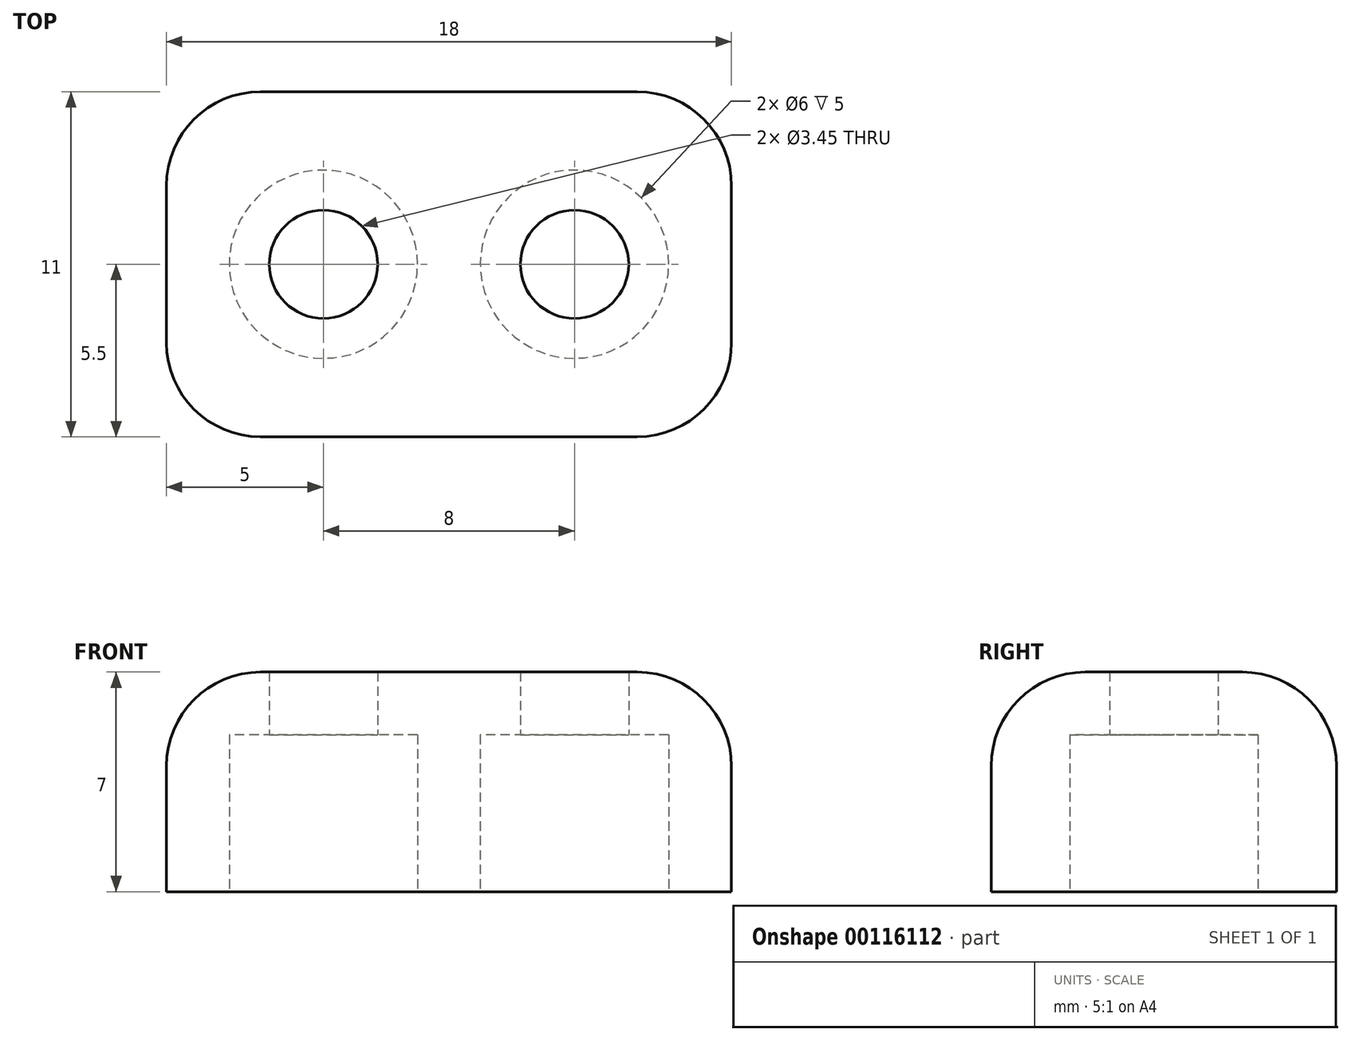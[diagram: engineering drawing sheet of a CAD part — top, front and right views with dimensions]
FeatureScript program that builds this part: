
annotation { "Feature Type Name" : "Feature", "Feature Type Description" : "" }
export const myFeature = defineFeature(function(context is Context, id is Id, definition is map)
    precondition{}
    {
        {
            var Q0;
            Q0=qCreatedBy(makeId("Top.planeOp"),FACE);
            var sketch = newSketch(context, id + "F0", { "sketchPlane" : qUnion([Q0])});
            skCircle(sketch, "E0", {"center": v(-4, 0) * mm, "radius": 3 * mm});
            skCircle(sketch, "E1", {"center": v(4, 0) * mm, "radius": 3 * mm});
            skLineSegment(sketch, "E2.bottom", {"start": v(9, 5.5) * mm, "end": v(-9, 5.5) * mm});
            skLineSegment(sketch, "E2.top", {"start": v(9, -5.5) * mm, "end": v(-9, -5.5) * mm});
            skLineSegment(sketch, "E2.left", {"start": v(9, 5.5) * mm, "end": v(9, -5.5) * mm});
            skLineSegment(sketch, "E2.right", {"start": v(-9, 5.5) * mm, "end": v(-9, -5.5) * mm});
            skPoint(sketch, "E2.middle", {"position": v(0, 0) * mm});
            skSolve(sketch);
        }
        {
            var Q0;
            Q0 = qSketchRegion(id + "F0", true);
            extrude(context, id + "F1", {"entities" : qUnion([Q0]), "depth" : 5 * mm});
        }
        {
            var Q0;
            Q0=makeQuery(id+"F1.opExtrude","CAP_FACE",FACE,{"disambiguationData":[OSD([sQuery(id+"F0.wireOp",EDGE,"E0"),sQuery(id+"F0.wireOp",EDGE,"E1"),sQuery(id+"F0.wireOp",EDGE,"E2.bottom"),sQuery(id+"F0.wireOp",EDGE,"E2.top"),sQuery(id+"F0.wireOp",EDGE,"E2.left"),sQuery(id+"F0.wireOp",EDGE,"E2.right")])],"isStart":false});
            var sketch = newSketch(context, id + "F2", { "sketchPlane" : qUnion([Q0])});
            skLineSegment(sketch, "E3.bottom", {"start": v(-9, 5.5) * mm, "end": v(9, 5.5) * mm});
            skLineSegment(sketch, "E3.top", {"start": v(-9, -5.5) * mm, "end": v(9, -5.5) * mm});
            skLineSegment(sketch, "E3.left", {"start": v(-9, 5.5) * mm, "end": v(-9, -5.5) * mm});
            skLineSegment(sketch, "E3.right", {"start": v(9, 5.5) * mm, "end": v(9, -5.5) * mm});
            skSolve(sketch);
        }
        {
            var Q0;
            Q0 = qSketchRegion(id + "F2", true);
            extrude(context, id + "F3", {"entities" : qUnion([Q0]), "operationType" : NewBodyOperationType.ADD, "depth" : 2 * mm});
        }
        {
            var Q0;
            Q0=makeQuery(id+"F3.boolean.opBoolean","MERGE",EDGE,{"derivedFrom":[makeQuery(id+"F1.opExtrude","SWEPT_EDGE",EDGE,{"disambiguationData":[OSD([sQuery(id+"F0.wireOp",EDGE,"E2.bottom"),sQuery(id+"F0.wireOp",EDGE,"E2.right")])]}),makeQuery(id+"F3.opExtrude","SWEPT_EDGE",EDGE,{"disambiguationData":[OSD([sQuery(id+"F2.wireOp",EDGE,"E3.bottom"),sQuery(id+"F2.wireOp",EDGE,"E3.left")])]})]});
            var Q1;
            Q1=makeQuery(id+"F3.boolean.opBoolean","MERGE",EDGE,{"derivedFrom":[makeQuery(id+"F1.opExtrude","SWEPT_EDGE",EDGE,{"disambiguationData":[OSD([sQuery(id+"F0.wireOp",EDGE,"E2.top"),sQuery(id+"F0.wireOp",EDGE,"E2.right")])]}),makeQuery(id+"F3.opExtrude","SWEPT_EDGE",EDGE,{"disambiguationData":[OSD([sQuery(id+"F2.wireOp",EDGE,"E3.top"),sQuery(id+"F2.wireOp",EDGE,"E3.left")])]})]});
            var Q2;
            Q2=makeQuery(id+"F3.boolean.opBoolean","MERGE",EDGE,{"derivedFrom":[makeQuery(id+"F1.opExtrude","SWEPT_EDGE",EDGE,{"disambiguationData":[OSD([sQuery(id+"F0.wireOp",EDGE,"E2.top"),sQuery(id+"F0.wireOp",EDGE,"E2.left")])]}),makeQuery(id+"F3.opExtrude","SWEPT_EDGE",EDGE,{"disambiguationData":[OSD([sQuery(id+"F2.wireOp",EDGE,"E3.top"),sQuery(id+"F2.wireOp",EDGE,"E3.right")])]})]});
            var Q3;
            Q3=makeQuery(id+"F3.boolean.opBoolean","MERGE",EDGE,{"derivedFrom":[makeQuery(id+"F1.opExtrude","SWEPT_EDGE",EDGE,{"disambiguationData":[OSD([sQuery(id+"F0.wireOp",EDGE,"E2.bottom"),sQuery(id+"F0.wireOp",EDGE,"E2.left")])]}),makeQuery(id+"F3.opExtrude","SWEPT_EDGE",EDGE,{"disambiguationData":[OSD([sQuery(id+"F2.wireOp",EDGE,"E3.bottom"),sQuery(id+"F2.wireOp",EDGE,"E3.right")])]})]});
            var Q4;
            Q4=makeQuery(id+"F3.opExtrude","CAP_EDGE",EDGE,{"disambiguationData":[OSD([sQuery(id+"F2.wireOp",EDGE,"E3.bottom")])],"isStart":false});
            var Q5;
            Q5=makeQuery(id+"F3.opExtrude","CAP_EDGE",EDGE,{"disambiguationData":[OSD([sQuery(id+"F2.wireOp",EDGE,"E3.top")])],"isStart":false});
            var Q6;
            Q6=makeQuery(id+"F3.opExtrude","CAP_EDGE",EDGE,{"disambiguationData":[OSD([sQuery(id+"F2.wireOp",EDGE,"E3.left")])],"isStart":false});
            var Q7;
            Q7=makeQuery(id+"F3.opExtrude","CAP_EDGE",EDGE,{"disambiguationData":[OSD([sQuery(id+"F2.wireOp",EDGE,"E3.right")])],"isStart":false});
            fillet(context, id + "F4", {"entities" : qUnion([Q0, Q1, Q2, Q3, Q4, Q5, Q6, Q7]), "radius" : 3 * mm, "tangentPropagation" : true, "allowEdgeOverflow" : false});
        }
        {
            var Q0;
            Q0=makeQuery(id+"F3.boolean.opBoolean","SPLIT",FACE,{"disambiguationData":[TD([makeQuery(id+"F1.opExtrude","SWEPT_FACE",FACE,{"disambiguationData":[OSD([sQuery(id+"F0.wireOp",EDGE,"E0")])]})])],"derivedFrom":makeQuery(id+"F3.opExtrude","CAP_FACE",FACE,{"disambiguationData":[OSD([sQuery(id+"F2.wireOp",EDGE,"E3.bottom"),sQuery(id+"F2.wireOp",EDGE,"E3.top"),sQuery(id+"F2.wireOp",EDGE,"E3.left"),sQuery(id+"F2.wireOp",EDGE,"E3.right")])],"isStart":true})});
            var sketch = newSketch(context, id + "F5", { "sketchPlane" : qUnion([Q0])});
            skCircle(sketch, "E4", {"center": v(-4, 0) * mm, "radius": 1.73 * mm});
            skCircle(sketch, "E5", {"center": v(4, 0) * mm, "radius": 1.73 * mm});
            skSolve(sketch);
        }
        {
            var Q0;
            Q0=makeQuery(id+"F5.imprint","IMPRINT",FACE,{"disambiguationData":[TD([[makeQuery(id+"F5.imprint","IMPRINT",EDGE,{"derivedFrom":sQuery(id+"F5.wireOp",EDGE,"E4")}),1.0]])]});
            var Q1;
            Q1=makeQuery(id+"F5.imprint","IMPRINT",FACE,{"disambiguationData":[TD([[makeQuery(id+"F5.imprint","IMPRINT",EDGE,{"derivedFrom":sQuery(id+"F5.wireOp",EDGE,"E5")}),1.0]])]});
            extrude(context, id + "F6", {"entities" : qUnion([Q0, Q1]), "operationType" : NewBodyOperationType.REMOVE, "oppositeDirection" : true, "depth" : 25 * mm});
        }
    });
